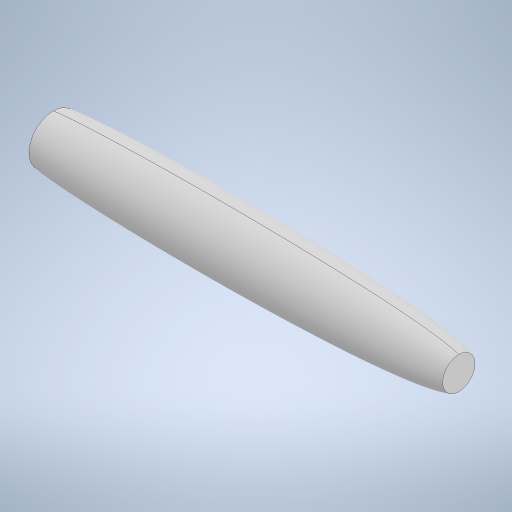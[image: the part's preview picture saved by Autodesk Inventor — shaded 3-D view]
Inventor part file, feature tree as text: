
AUTODESK INVENTOR PART (.ipt)
format: ipt  version: 2023 (Build 270158030, 158C)  size: 278,016 bytes
history: native  units: mm
features: revolve x1, sketch x1
ambient origin geometry x8: Origin, YZ Plane, XZ Plane, XY Plane, X Axis, Y Axis, Z Axis, Center Point
bodies: Solid1 (feature_tree)
feature tree (2):
  revolve  "Revolution1"  [1 undecoded]
  sketch  "Sketch3"  dims[d1=100.0mm d2=6.0mm d3=4.0mm d4=7.0mm d5=8.0mm d6=8.0mm d7=38.0mm d8=20.0mm d9=43.0mm d10=50.0mm d11=90.0deg]
note: 1 required parameter value undecoded (feature->parameter linkage not recoverable at this tier; creation-order binding heuristic only, values carry confidence <= 0.55)
